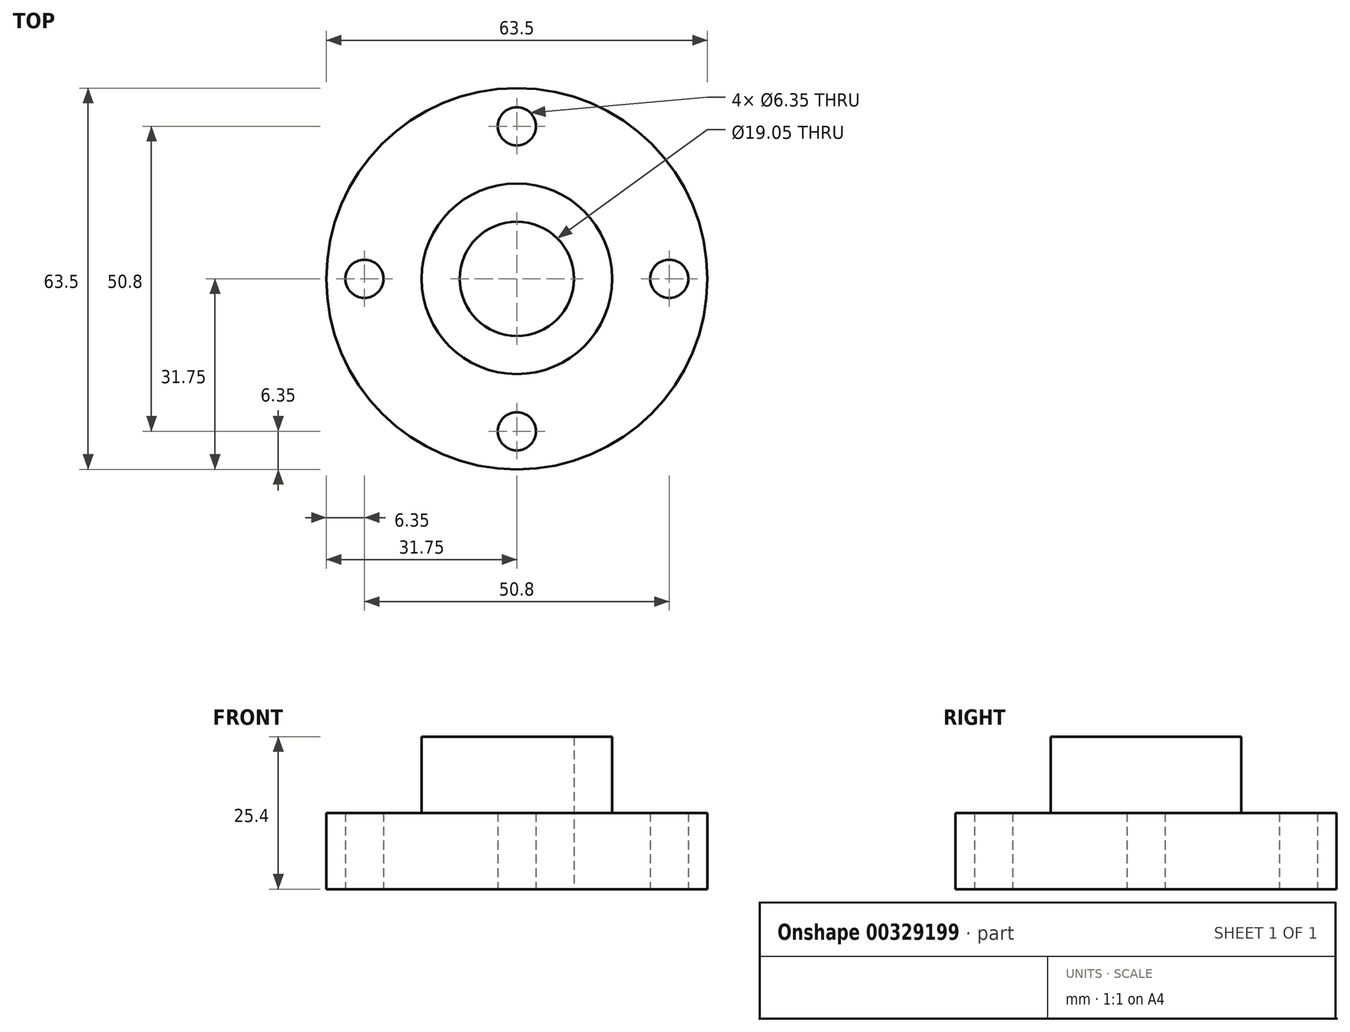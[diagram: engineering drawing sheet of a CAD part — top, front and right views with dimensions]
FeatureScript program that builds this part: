
annotation { "Feature Type Name" : "Feature", "Feature Type Description" : "" }
export const myFeature = defineFeature(function(context is Context, id is Id, definition is map)
    precondition{}
    {
        {
            var Q0;
            Q0=qCreatedBy(makeId("Top.planeOp"),FACE);
            var sketch = newSketch(context, id + "F0", { "sketchPlane" : qUnion([Q0])});
            skCircle(sketch, "E0", {"center": v(0, 0) * mm, "radius": 15.88 * mm});
            skCircle(sketch, "E1", {"center": v(0, 0) * mm, "radius": 31.75 * mm});
            skCircle(sketch, "E2", {"center": v(0, 25.4) * mm, "radius": 3.18 * mm});
            skCircle(sketch, "E3", {"center": v(25.4, 0) * mm, "radius": 3.18 * mm});
            skCircle(sketch, "E4", {"center": v(0, -25.4) * mm, "radius": 3.18 * mm});
            skCircle(sketch, "E5", {"center": v(-25.4, 0) * mm, "radius": 3.18 * mm});
            skSolve(sketch);
        }
        {
            var Q0;
            Q0 = qSketchRegion(id + "F0", true);
            extrude(context, id + "F1", {"entities" : qUnion([Q0]), "depth" : 12.7 * mm});
        }
        {
            var Q0;
            Q0=makeQuery(id+"F0.imprint","IMPRINT",FACE,{"disambiguationData":[TD([[makeQuery(id+"F0.imprint","IMPRINT",EDGE,{"derivedFrom":sQuery(id+"F0.wireOp",EDGE,"E0")}),1.0]])]});
            extrude(context, id + "F2", {"entities" : qUnion([Q0]), "operationType" : NewBodyOperationType.ADD, "depth" : 25.4 * mm});
        }
        {
            var Q0;
            Q0=qCreatedBy(makeId("Top.planeOp"),FACE);
            var sketch = newSketch(context, id + "F3", { "sketchPlane" : qUnion([Q0])});
            skCircle(sketch, "E6", {"center": v(0, 0) * mm, "radius": 9.53 * mm});
            skSolve(sketch);
        }
        {
            var Q0;
            Q0 = qSketchRegion(id + "F3", true);
            extrude(context, id + "F4", {"entities" : qUnion([Q0]), "operationType" : NewBodyOperationType.REMOVE, "endBound" : BoundingType.THROUGH_ALL, "depth" : 25.4 * mm});
        }
    });
